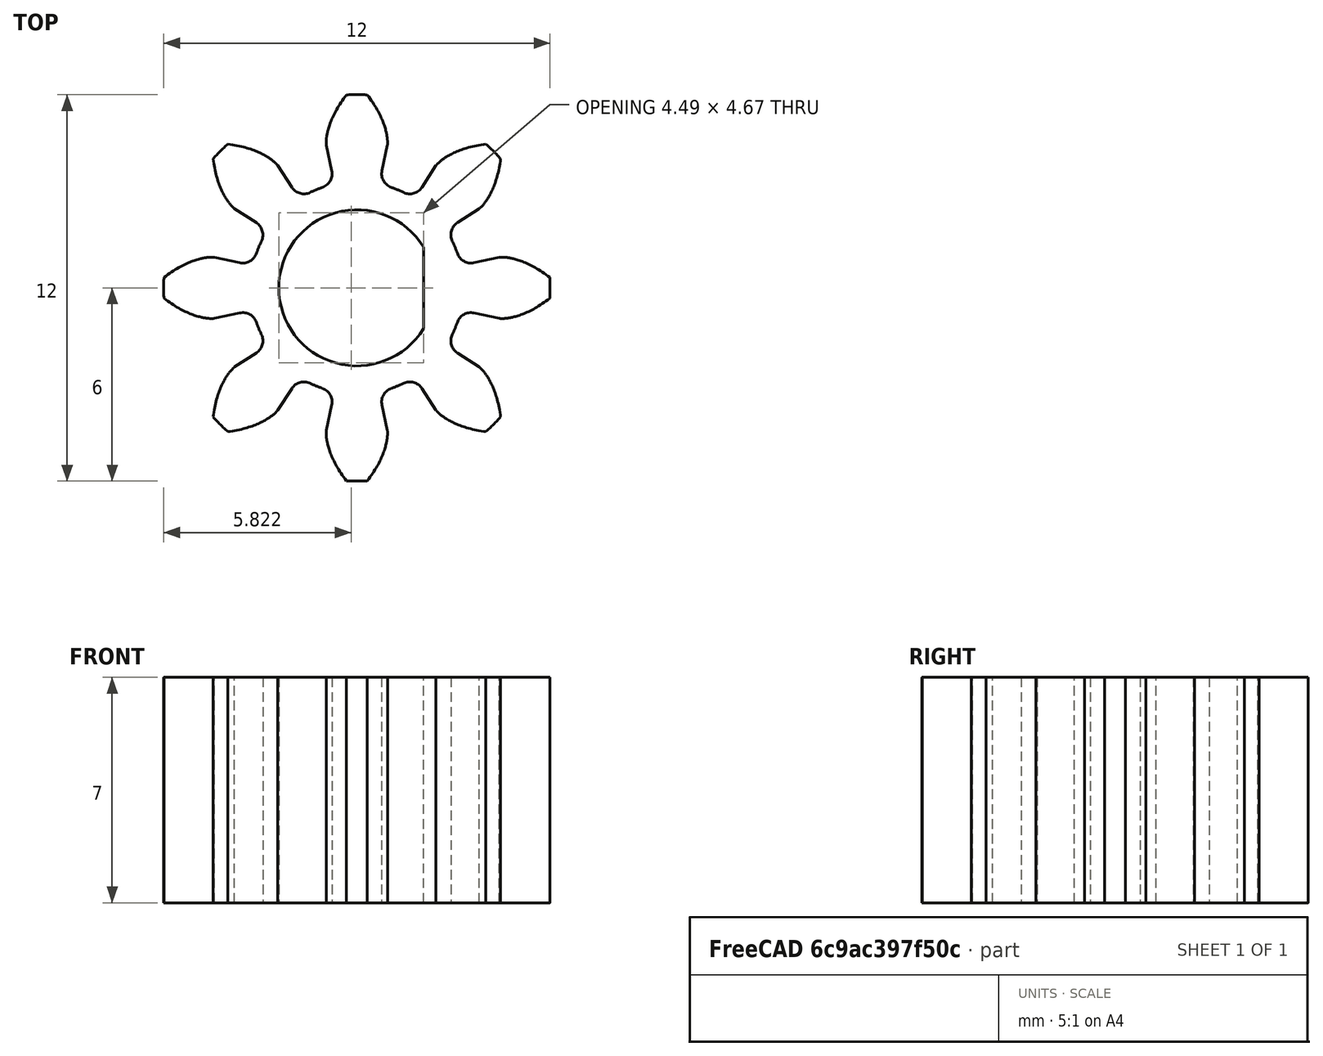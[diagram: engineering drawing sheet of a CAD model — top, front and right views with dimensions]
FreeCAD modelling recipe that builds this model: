
FCSTD DOCUMENT  (FreeCAD 0.16R6712 (Git))
Label: mini-gear
License: All rights reserved
LicenseURL: http://en.wikipedia.org/wiki/All_rights_reserved
objects: Part::Extrusion×2, Part::Part2DObjectPython×1, Sketcher::SketchObject×1, Part::Cut×1
note: 5 computed .brp shape members not serialized (recipe doc carries the construction recipe); baked Part::Feature solids carry a one-line shape summary decoded from their .brp

FEATURE [Part::Part2DObjectPython] InvoluteGear  # Draft 2D object (typed FeaturePython)
  ExternalGear = true
  HighPrecision = true
  Modules = 1.2
  NumberOfTeeth = 8
  PressureAngle = 20
FEATURE [Sketcher::SketchObject] Sketch
  sketch-geometry (2):
    g0: ArcOfCircle CenterX=0 CenterY=0 CenterZ=0 NormalX=0 NormalY=0 NormalZ=1 Radius=2.42475 StartAngle=0.549584 EndAngle=5.7336
    g1: LineSegment StartX=2.06769 StartY=1.26653 StartZ=0 EndX=2.06769 EndY=-1.26653 EndZ=0
  constraints (3):
    c: Coincident(g0,g-1)
    c: Coincident(g1,g0)
    c: Coincident(g1,g0)
FEATURE [Part::Extrusion] Extrude
  Base = -> InvoluteGear
  Dir = (0,0,7)
  Solid = true
FEATURE [Part::Extrusion] Extrude001
  Base = -> Sketch
  Dir = (0,0,7)
  Solid = true
FEATURE [Part::Cut] Cut
  Base = -> Extrude
  Tool = -> Extrude001
